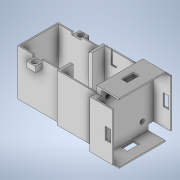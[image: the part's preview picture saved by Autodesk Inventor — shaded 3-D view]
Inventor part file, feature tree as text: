
AUTODESK INVENTOR PART (.ipt)
format: ipt  version: 2020.2 (Build 242310000, 310)  size: 493,056 bytes
history: native  units: in
note: dims shown in document units (in); Inventor stores cm internally (conversion verified against a paired STEP export)
features: extrude x22, sketch x21, projected_geometry x11, hole x1
ambient origin geometry x8: Origin, YZ Plane, XZ Plane, XY Plane, X Axis, Y Axis, Z Axis, Center Point
bodies: Solid1 (feature_tree)
feature tree (55):
  extrude  "Extrusion1"  TaperAngle=180.0deg  [1 undecoded]
  extrude  "Extrusion3"  Depth=0.0787in TaperAngle=0.0deg
  extrude  "Extrusion4"  Depth=0.0394in
  extrude  "Extrusion5"  Depth=0.0394in
  extrude  "Extrusion6"  Depth=0.3126in
  extrude  "Extrusion8"  Depth=0.0787in TaperAngle=0.0deg
  extrude  "Extrusion9"  Depth=0.689in
  sketch  "Sketch9"  dims[d19=1.378in d20=0.1575in]
  extrude  "Extrusion11"  Depth=0.1575in
  extrude  "Extrusion13"  Depth=0.1378in
  extrude  "Extrusion14"  Depth=0.2756in
  extrude  "Extrusion16"  Depth=0.1575in TaperAngle=0.0deg
  sketch  "Sketch17"  dims[d28=0.0787in d29=0.0in d33=0.6496in]
  sketch  "Sketch18"  dims[d34=0.0in d35=1.2992in]
  extrude  "Extrusion17"  Depth=0.6496in
  extrude  "Extrusion18"  Depth=1.2992in
  extrude  "Extrusion19"  Depth=0.0787in TaperAngle=0.0deg
  sketch  "Sketch20"  dims[d39=0.0394in d40=0.0394in]
  extrude  "Extrusion20"  Depth=0.0394in
  extrude  "Extrusion21"  Depth=1.378in
  extrude  "Extrusion22"  Depth=1.2205in TaperAngle=0.0deg
  extrude  "Extrusion23"  Depth=0.0787in TaperAngle=0.0deg
  hole  "Hole1"  [1 undecoded]
  extrude  "Extrusion24"  Depth=1.1693in
  extrude  "Extrusion25"  Depth=0.3937in
  extrude  "Extrusion26"  TaperAngle=90.0deg  [1 undecoded]
  extrude  "Extrusion27"  Depth=0.1969in
  sketch  "Sketch1"  dims[d0=1.2599in d1=180.0deg]
  sketch  "Sketch2"  dims[d2=1.2in d3=0.0787in d4=0.0in]
  projected_geometry  "Projected Loop1"
  sketch  "Sketch3"  dims[d5=0.0394in d6=0.0394in]
  sketch  "Sketch4"  dims[d7=0.0394in d8=0.0394in]
  sketch  "Sketch5"  dims[d11=0.3126in d12=0.3126in]
  projected_geometry  "Projected Loop2"
  sketch  "Sketch7"  dims[d13=1.1811in d14=0.0in d15=0.0787in d16=0.0in]
  sketch  "Sketch8"  dims[d17=0.6693in d18=0.689in]
  projected_geometry  "Projected Loop4"
  sketch  "Sketch10"  dims[d21=0.1575in d22=0.1378in]
  sketch  "Sketch14"  dims[d23=0.1969in d24=0.2756in]
  projected_geometry  "Projected Loop5"
  sketch  "Sketch15"  dims[d25=0.1969in d26=0.1575in d27=0.0in]
  projected_geometry  "Projected Loop6"
  projected_geometry  "Projected Loop7"
  sketch  "Sketch19"  dims[d36=1.378in d37=0.0787in d38=0.0in]
  projected_geometry  "Projected Loop8"
  projected_geometry  "Projected Loop9"
  sketch  "Sketch21"  dims[d41=1.4567in d42=1.378in]
  sketch  "Sketch22"  dims[d43=1.1811in d44=0.0in d47=1.2205in d48=0.0in]
  sketch  "Sketch23"  dims[d57=0.3937in d58=0.0in d59=0.0787in d60=0.0in]
  projected_geometry  "Projected Loop10"
  projected_geometry  "Projected Loop11"
  sketch  "Sketch24"  dims[d67=0.0787in d68=0.0in d69=0.1181in]
  projected_geometry  "Projected Loop12"
  sketch  "Sketch25"  dims[d70=0.0728in d71=1.1693in]
  sketch  "Sketch26"  dims[d72=1.1535in d73=1.1693in d74=90.0deg d75=0.1969in d76=0.1969in d77=0.0394in d78=0.0394in d79=0.0394in d80=0.0394in d81=0.0787in d82=0.0in d83=0.5906in d84=0.0in d85=0.0787in d86=0.0in d87=0.1969in d88=0.1575in d89=0.1969in d90=0.0394in d91=0.5906in d92=0.0in d93=0.0787in d94=0.0in d95=0.7087in d96=0.0394in d97=0.1772in d98=0.1772in d99=0.3543in d100=0.0in d101=0.0in d102=0.7087in d103=0.0787in d104=0.1654in d105=0.0394in d106=0.1772in d107=0.1772in d108=0.1772in d109=0.3543in d110=0.0in d111=0.0in d112=0.065in d113=0.063in d114=0.063in d115=0.065in d116=0.1339in d117=0.2362in d118=0.1575in d119=0.0787in d120=90.0deg d121=0.315in d122=0.8108in d123=0.0787in d124=0.0in d125=0.0787in d126=0.0in d127=0.8661in d128=0.0394in d129=0.3937in d130=0.0in d131=0.1181in d132=0.0394in d133=0.3937in d134=0.0in]
note: 3 required parameter values undecoded (feature->parameter linkage not recoverable at this tier; creation-order binding heuristic only, values carry confidence <= 0.55)
